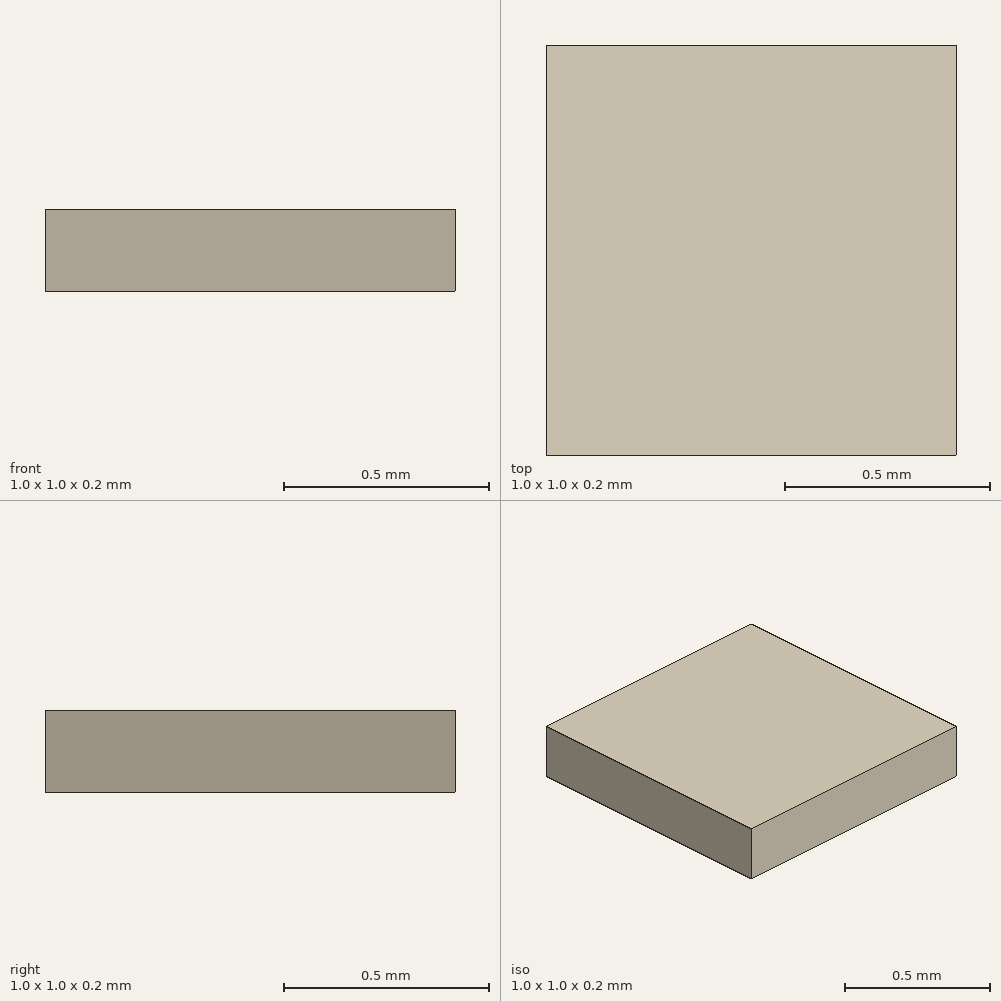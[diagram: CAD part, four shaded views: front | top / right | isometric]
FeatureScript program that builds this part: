
annotation { "Feature Type Name" : "Feature", "Feature Type Description" : "" }
export const myFeature = defineFeature(function(context is Context, id is Id, definition is map)
    precondition{}
    {
        {
            var Q0;
            Q0=qCreatedBy(makeId("Top.planeOp"),FACE);
            var sketch = newSketch(context, id + "F0", { "sketchPlane" : qUnion([Q0])});
            skLineSegment(sketch, "E0.bottom", {"start": v(-0.5, 0.5) * mm, "end": v(0.5, 0.5) * mm});
            skLineSegment(sketch, "E0.top", {"start": v(-0.5, -0.5) * mm, "end": v(0.5, -0.5) * mm});
            skLineSegment(sketch, "E0.left", {"start": v(-0.5, 0.5) * mm, "end": v(-0.5, -0.5) * mm});
            skLineSegment(sketch, "E0.right", {"start": v(0.5, 0.5) * mm, "end": v(0.5, -0.5) * mm});
            skPoint(sketch, "E0.middle", {"position": v(0, 0) * mm});
            skSolve(sketch);
        }
        {
            var Q0;
            Q0 = qSketchRegion(id + "F0", true);
            extrude(context, id + "F1", {"entities" : qUnion([Q0]), "depth" : 0.2 * mm, "offsetDistance" : 25.4 * mm});
        }
    });
